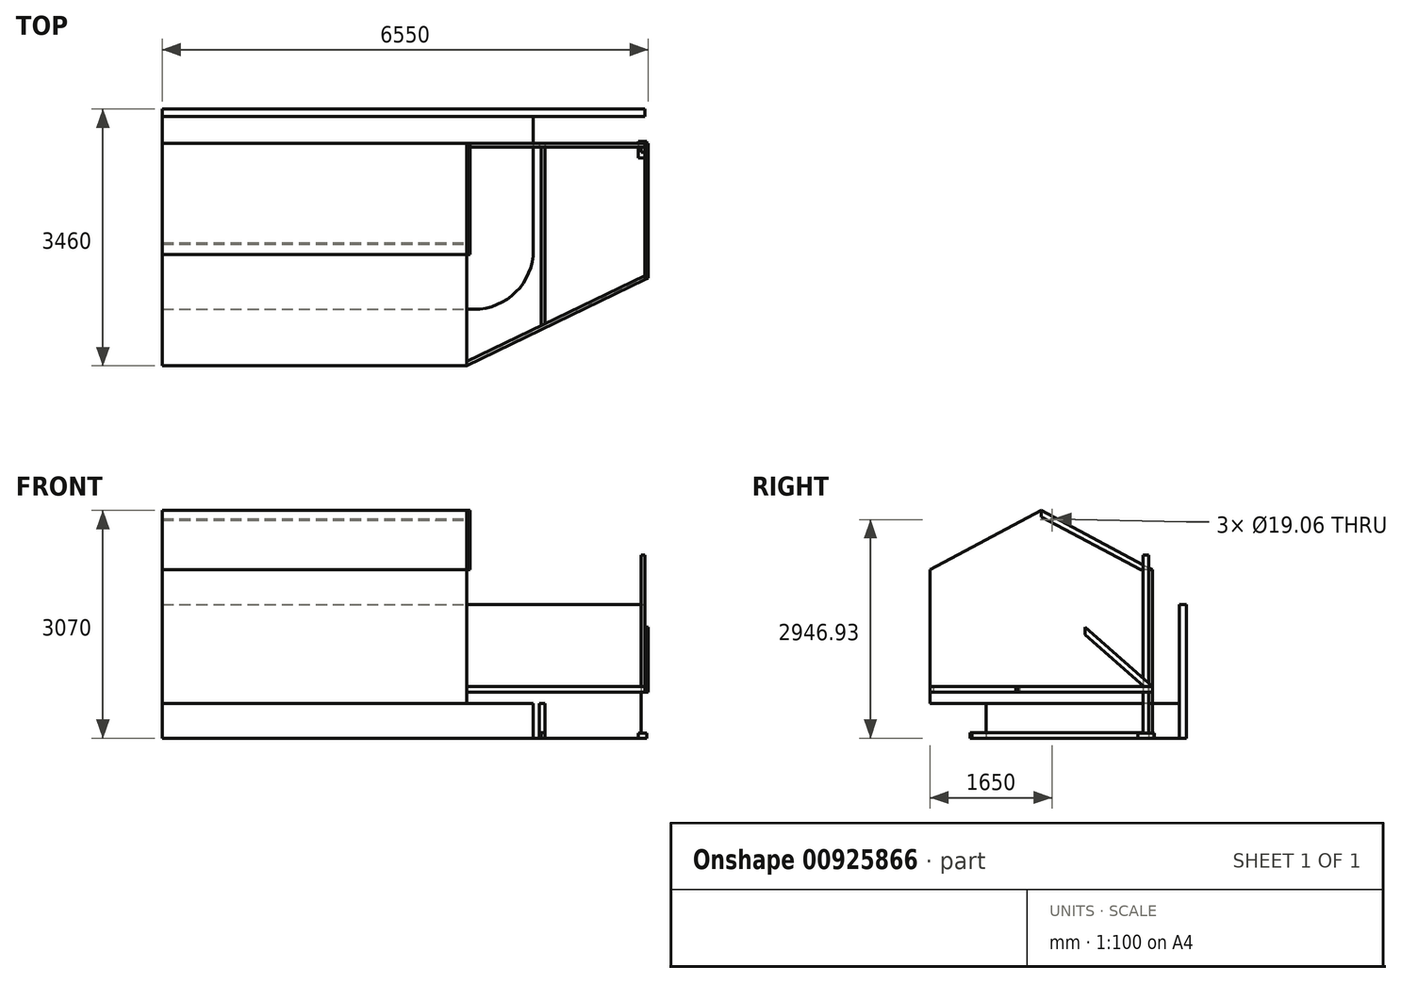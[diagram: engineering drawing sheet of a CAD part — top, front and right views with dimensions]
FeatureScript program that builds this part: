
annotation { "Feature Type Name" : "Feature", "Feature Type Description" : "" }
export const myFeature = defineFeature(function(context is Context, id is Id, definition is map)
    precondition{}
    {
        {
            var Q0;
            Q0=qCreatedBy(makeId("Top.planeOp"),FACE);
            var sketch = newSketch(context, id + "F0", { "sketchPlane" : qUnion([Q0])});
            skLineSegment(sketch, "E0.bottom", {"start": v(0, 0) * mm, "end": v(6500, 0) * mm});
            skLineSegment(sketch, "E0.top", {"start": v(0, 100) * mm, "end": v(6500, 100) * mm});
            skLineSegment(sketch, "E0.left", {"start": v(0, 0) * mm, "end": v(0, 100) * mm});
            skLineSegment(sketch, "E0.right", {"start": v(6500, 0) * mm, "end": v(6500, 100) * mm});
            skSolve(sketch);
        }
        {
            var Q0;
            Q0 = qSketchRegion(id + "F0", true);
            extrude(context, id + "F1", {"entities" : qUnion([Q0]), "depth" : 1800 * mm, "offsetDistance" : 25 * mm});
        }
        {
            var Q0;
            Q0=qCreatedBy(makeId("Top.planeOp"),FACE);
            var sketch = newSketch(context, id + "F2", { "sketchPlane" : qUnion([Q0])});
            skLineSegment(sketch, "E1.bottom", {"start": v(0, 0) * mm, "end": v(5000, 0) * mm});
            skLineSegment(sketch, "E1.top", {"start": v(0, -2600) * mm, "end": v(4200, -2600) * mm});
            skLineSegment(sketch, "E1.left", {"start": v(0, 0) * mm, "end": v(0, -2600) * mm});
            skLineSegment(sketch, "E1.right", {"start": v(5000, 0) * mm, "end": v(5000, -1800) * mm});
            skPoint(sketch, "E2.visualSharp", {"position": v(5000, -2600) * mm});
            skArc(sketch, "E2.filletArc", {"start": v(4200, -2600) * mm, "mid": v(4765.69, -2365.69) * mm, "end": v(5000, -1800) * mm});
            skSolve(sketch);
        }
        {
            var Q0;
            Q0 = qSketchRegion(id + "F2", true);
            extrude(context, id + "F3", {"entities" : qUnion([Q0]), "depth" : 470 * mm, "offsetDistance" : 25 * mm});
        }
        {
            var Q0;
            Q0=makeQuery(id+"F3.opExtrude","CAP_FACE",FACE,{"disambiguationData":[OSD([sQuery(id+"F2.wireOp",EDGE,"E1.bottom"),sQuery(id+"F2.wireOp",EDGE,"E1.top"),sQuery(id+"F2.wireOp",EDGE,"E1.left"),sQuery(id+"F2.wireOp",EDGE,"E1.right"),sQuery(id+"F2.wireOp",EDGE,"E2.filletArc")])],"isStart":false});
            var sketch = newSketch(context, id + "F4", { "sketchPlane" : qUnion([Q0])});
            skLineSegment(sketch, "E3.bottom", {"start": v(0, -3360) * mm, "end": v(4100, -3360) * mm});
            skLineSegment(sketch, "E3.top", {"start": v(0, -360) * mm, "end": v(4100, -360) * mm});
            skLineSegment(sketch, "E3.left", {"start": v(0, -3360) * mm, "end": v(0, -360) * mm});
            skLineSegment(sketch, "E3.right", {"start": v(4100, -3360) * mm, "end": v(4100, -360) * mm});
            skSolve(sketch);
        }
        {
            var Q0;
            Q0 = qSketchRegion(id + "F4", true);
            extrude(context, id + "F5", {"entities" : qUnion([Q0]), "depth" : 1800 * mm, "offsetDistance" : 25 * mm});
        }
        {
            var Q0;
            Q0=makeQuery(id+"F5.opExtrude","SWEPT_FACE",FACE,{"disambiguationData":[OSD([sQuery(id+"F4.wireOp",EDGE,"E3.right")])]});
            var sketch = newSketch(context, id + "F6", { "sketchPlane" : qUnion([Q0])});
            skLineSegment(sketch, "E4", {"start": v(-3360, 2270) * mm, "end": v(-1860, 3070) * mm});
            skPoint(sketch, "E4.endSnap0", {"position": v(-1860, 2270) * mm});
            skLineSegment(sketch, "E5", {"start": v(-1860, 3070) * mm, "end": v(-360, 2270) * mm});
            skLineSegment(sketch, "E6.0", {"start": v(-3360, 2270) * mm, "end": v(-360, 2270) * mm});
            skSolve(sketch);
        }
        {
            var Q0;
            Q0 = qSketchRegion(id + "F6", true);
            var Q1;
            Q1=makeQuery(id+"F5.opExtrude","SWEPT_FACE",FACE,{"disambiguationData":[OSD([sQuery(id+"F4.wireOp",EDGE,"E3.left")])]});
            extrude(context, id + "F7", {"entities" : qUnion([Q0]), "operationType" : NewBodyOperationType.ADD, "endBound" : BoundingType.UP_TO_SURFACE, "oppositeDirection" : true, "depth" : 25 * mm, "endBoundEntityFace" : qUnion([Q1]), "offsetDistance" : 25 * mm});
        }
        {
            var Q0;
            Q0=qCreatedBy(makeId("Top.planeOp"),FACE);
            var sketch = newSketch(context, id + "F8", { "sketchPlane" : qUnion([Q0])});
            skLineSegment(sketch, "E7.bottom", {"start": v(5000, 0) * mm, "end": v(6500, 0) * mm});
            skLineSegment(sketch, "E7.top", {"start": v(5000, -2200) * mm, "end": v(6500, -2200) * mm});
            skLineSegment(sketch, "E7.left", {"start": v(5000, 0) * mm, "end": v(5000, -2200) * mm});
            skLineSegment(sketch, "E7.right", {"start": v(6500, 0) * mm, "end": v(6500, -2200) * mm});
            skLineSegment(sketch, "E8", {"start": v(4100, -3360) * mm, "end": v(6500, -2200) * mm});
            skSolve(sketch);
        }
        {
            var Q0;
            Q0=makeQuery(id+"F7.boolean.opBoolean","MERGE",FACE,{"derivedFrom":[makeQuery(id+"F5.opExtrude","SWEPT_FACE",FACE,{"disambiguationData":[OSD([sQuery(id+"F4.wireOp",EDGE,"E3.right")])]}),makeQuery(id+"F7.opExtrude","CAP_FACE",FACE,{"disambiguationData":[OSD([sQuery(id+"F6.wireOp",EDGE,"E4"),sQuery(id+"F6.wireOp",EDGE,"E5"),sQuery(id+"F6.wireOp",EDGE,"E6.0")])],"isStart":true})]});
            var sketch = newSketch(context, id + "F9", { "sketchPlane" : qUnion([Q0])});
            skLineSegment(sketch, "E9.bottom", {"start": v(-360, 620) * mm, "end": v(-410, 620) * mm});
            skLineSegment(sketch, "E9.top", {"start": v(-360, 696) * mm, "end": v(-410, 696) * mm});
            skLineSegment(sketch, "E9.left", {"start": v(-360, 620) * mm, "end": v(-360, 696) * mm});
            skLineSegment(sketch, "E9.right", {"start": v(-410, 620) * mm, "end": v(-410, 696) * mm});
            skSolve(sketch);
        }
        {
            var Q0;
            Q0 = qSketchRegion(id + "F9", true);
            extrude(context, id + "F10", {"entities" : qUnion([Q0]), "depth" : 2400 * mm, "offsetDistance" : 25 * mm});
        }
        {
            var Q0;
            Q0=makeQuery(id+"F10.opExtrude","SWEPT_FACE",FACE,{"disambiguationData":[OSD([sQuery(id+"F9.wireOp",EDGE,"E9.top")])]});
            var sketch = newSketch(context, id + "F11", { "sketchPlane" : qUnion([Q0])});
            skLineSegment(sketch, "E10", {"start": v(4100, -3304.47) * mm, "end": v(4100, -3360) * mm});
            skLineSegment(sketch, "E11", {"start": v(4100, -3360) * mm, "end": v(6500, -2200) * mm});
            skLineSegment(sketch, "E12", {"start": v(6500, -2200) * mm, "end": v(6500, -2144.47) * mm});
            skLineSegment(sketch, "E13", {"start": v(6500, -2144.47) * mm, "end": v(4100, -3304.47) * mm});
            skSolve(sketch);
        }
        {
            var Q0;
            Q0 = qSketchRegion(id + "F11", true);
            extrude(context, id + "F12", {"entities" : qUnion([Q0]), "oppositeDirection" : true, "depth" : 76 * mm, "offsetDistance" : 25 * mm});
        }
        {
            var Q0;
            Q0=makeQuery(id+"F10.opExtrude","CAP_FACE",FACE,{"disambiguationData":[OSD([sQuery(id+"F9.wireOp",EDGE,"E9.bottom"),sQuery(id+"F9.wireOp",EDGE,"E9.top"),sQuery(id+"F9.wireOp",EDGE,"E9.left"),sQuery(id+"F9.wireOp",EDGE,"E9.right")])],"isStart":false});
            var sketch = newSketch(context, id + "F13", { "sketchPlane" : qUnion([Q0])});
            skLineSegment(sketch, "E14.bottom", {"start": v(-360, 620) * mm, "end": v(-2200, 620) * mm});
            skLineSegment(sketch, "E14.top", {"start": v(-360, 696) * mm, "end": v(-2200, 696) * mm});
            skLineSegment(sketch, "E14.left", {"start": v(-360, 620) * mm, "end": v(-360, 696) * mm});
            skLineSegment(sketch, "E14.right", {"start": v(-2200, 620) * mm, "end": v(-2200, 696) * mm});
            skSolve(sketch);
        }
        {
            var Q0;
            Q0 = qSketchRegion(id + "F13", true);
            extrude(context, id + "F14", {"entities" : qUnion([Q0]), "depth" : 50 * mm, "offsetDistance" : 25 * mm});
        }
        {
            var Q0;
            Q0=qCreatedBy(makeId("Top.planeOp"),FACE);
            var sketch = newSketch(context, id + "F15", { "sketchPlane" : qUnion([Q0])});
            skLineSegment(sketch, "E15.bottom", {"start": v(6526.6, -337.86) * mm, "end": v(6416.6, -337.86) * mm});
            skLineSegment(sketch, "E15.top", {"start": v(6526.6, -557.86) * mm, "end": v(6416.6, -557.86) * mm});
            skLineSegment(sketch, "E15.left", {"start": v(6526.6, -337.86) * mm, "end": v(6526.6, -557.86) * mm});
            skLineSegment(sketch, "E15.right", {"start": v(6416.6, -337.86) * mm, "end": v(6416.6, -557.86) * mm});
            skSolve(sketch);
        }
        {
            var Q0;
            Q0 = qSketchRegion(id + "F15", true);
            extrude(context, id + "F16", {"entities" : qUnion([Q0]), "depth" : 70 * mm, "offsetDistance" : 25 * mm});
        }
        {
            var Q0;
            Q0=makeQuery(id+"F16.opExtrude","CAP_FACE",FACE,{"disambiguationData":[OSD([sQuery(id+"F15.wireOp",EDGE,"E15.bottom"),sQuery(id+"F15.wireOp",EDGE,"E15.top"),sQuery(id+"F15.wireOp",EDGE,"E15.left"),sQuery(id+"F15.wireOp",EDGE,"E15.right")])],"isStart":false});
            var sketch = newSketch(context, id + "F17", { "sketchPlane" : qUnion([Q0])});
            skLineSegment(sketch, "E16.bottom", {"start": v(6500, -410) * mm, "end": v(6450, -410) * mm});
            skLineSegment(sketch, "E16.top", {"start": v(6500, -486) * mm, "end": v(6450, -486) * mm});
            skLineSegment(sketch, "E16.left", {"start": v(6500, -410) * mm, "end": v(6500, -486) * mm});
            skLineSegment(sketch, "E16.right", {"start": v(6450, -410) * mm, "end": v(6450, -486) * mm});
            skSolve(sketch);
        }
        {
            var Q0;
            Q0 = qSketchRegion(id + "F17", true);
            extrude(context, id + "F18", {"entities" : qUnion([Q0]), "depth" : 2400 * mm, "offsetDistance" : 25 * mm});
        }
        {
            var Q0;
            Q0=makeQuery(id+"F7.boolean.opBoolean","MERGE",FACE,{"derivedFrom":[makeQuery(id+"F5.opExtrude","SWEPT_FACE",FACE,{"disambiguationData":[OSD([sQuery(id+"F4.wireOp",EDGE,"E3.right")])]}),makeQuery(id+"F7.opExtrude","CAP_FACE",FACE,{"disambiguationData":[OSD([sQuery(id+"F6.wireOp",EDGE,"E4"),sQuery(id+"F6.wireOp",EDGE,"E5"),sQuery(id+"F6.wireOp",EDGE,"E6.0")])],"isStart":true})]});
            var sketch = newSketch(context, id + "F19", { "sketchPlane" : qUnion([Q0])});
            skLineSegment(sketch, "E17.0", {"start": v(-1860, 3070) * mm, "end": v(-360, 2270) * mm});
            skLineSegment(sketch, "E18.0", {"start": v(-1860, 2983.87) * mm, "end": v(-521.5, 2270) * mm});
            skLineSegment(sketch, "E19", {"start": v(-1860, 3070) * mm, "end": v(-1860, 2983.87) * mm});
            skLineSegment(sketch, "E20", {"start": v(-360, 2270) * mm, "end": v(-521.5, 2270) * mm});
            skSolve(sketch);
        }
        {
            var Q0;
            Q0 = qSketchRegion(id + "F19", true);
            extrude(context, id + "F20", {"entities" : qUnion([Q0]), "depth" : 50 * mm, "offsetDistance" : 25 * mm});
        }
        {
            var Q0;
            Q0=makeQuery(id+"F14.opExtrude","SWEPT_FACE",FACE,{"disambiguationData":[OSD([sQuery(id+"F13.wireOp",EDGE,"E14.top")])]});
            var sketch = newSketch(context, id + "F21", { "sketchPlane" : qUnion([Q0])});
            skLineSegment(sketch, "E21.0", {"start": v(6500, -2200) * mm, "end": v(6550, -2175.83) * mm});
            skLineSegment(sketch, "E22.0", {"start": v(6550, -2175.83) * mm, "end": v(6550, -2200) * mm});
            skLineSegment(sketch, "E23.0", {"start": v(6550, -2200) * mm, "end": v(6500, -2200) * mm});
            skPoint(sketch, "E24.orphan", {"position": v(6500, -2200) * mm});
            skPoint(sketch, "E25.orphan", {"position": v(4100, -3360) * mm});
            skPoint(sketch, "E26.orphan", {"position": v(6550, -360) * mm});
            skSolve(sketch);
        }
        {
            var Q0;
            Q0 = qSketchRegion(id + "F21", true);
            extrude(context, id + "F22", {"entities" : qUnion([Q0]), "operationType" : NewBodyOperationType.REMOVE, "endBound" : BoundingType.THROUGH_ALL, "oppositeDirection" : true, "depth" : 25 * mm, "offsetDistance" : 25 * mm});
        }
        {
            var Q0;
            Q0=makeQuery(id+"F14.opExtrude","CAP_FACE",FACE,{"disambiguationData":[OSD([sQuery(id+"F13.wireOp",EDGE,"E14.bottom"),sQuery(id+"F13.wireOp",EDGE,"E14.top"),sQuery(id+"F13.wireOp",EDGE,"E14.left"),sQuery(id+"F13.wireOp",EDGE,"E14.right")])],"isStart":false});
            var sketch = newSketch(context, id + "F23", { "sketchPlane" : qUnion([Q0])});
            skLineSegment(sketch, "E27", {"start": v(-360, 696) * mm, "end": v(-1267.92, 1496) * mm});
            skLineSegment(sketch, "E28", {"start": v(-1267.92, 1394.7) * mm, "end": v(-474.96, 696) * mm});
            skLineSegment(sketch, "E29.0", {"start": v(-360, 696) * mm, "end": v(-474.96, 696) * mm});
            skPoint(sketch, "E30.orphan", {"position": v(-2175.83, 696) * mm});
            skLineSegment(sketch, "E31", {"start": v(-1267.92, 1394.7) * mm, "end": v(-1267.92, 1496) * mm});
            skPoint(sketch, "E32.orphan", {"position": v(-1267.92, 696) * mm});
            skSolve(sketch);
        }
        {
            var Q0;
            Q0 = qSketchRegion(id + "F23", true);
            extrude(context, id + "F24", {"entities" : qUnion([Q0]), "oppositeDirection" : true, "depth" : 50 * mm, "offsetDistance" : 25 * mm});
        }
        {
            var Q0;
            Q0=qCreatedBy(makeId("Top.planeOp"),FACE);
            var sketch = newSketch(context, id + "F25", { "sketchPlane" : qUnion([Q0])});
            skLineSegment(sketch, "E33.bottom", {"start": v(5080, -360) * mm, "end": v(5156, -360) * mm});
            skLineSegment(sketch, "E33.top", {"start": v(5080, -410) * mm, "end": v(5156, -410) * mm});
            skLineSegment(sketch, "E33.left", {"start": v(5080, -360) * mm, "end": v(5080, -410) * mm});
            skLineSegment(sketch, "E33.right", {"start": v(5156, -360) * mm, "end": v(5156, -410) * mm});
            skSolve(sketch);
        }
        {
            var Q0;
            Q0 = qSketchRegion(id + "F25", true);
            extrude(context, id + "F26", {"entities" : qUnion([Q0]), "depth" : 470 * mm, "offsetDistance" : 25 * mm});
        }
        {
            var Q0;
            Q0=makeQuery(id+"F26.opExtrude","SWEPT_FACE",FACE,{"disambiguationData":[OSD([sQuery(id+"F25.wireOp",EDGE,"E33.top")])]});
            var sketch = newSketch(context, id + "F27", { "sketchPlane" : qUnion([Q0])});
            skLineSegment(sketch, "E34.bottom", {"start": v(5156, 0) * mm, "end": v(5106, 0) * mm});
            skLineSegment(sketch, "E34.top", {"start": v(5156, 76) * mm, "end": v(5106, 76) * mm});
            skLineSegment(sketch, "E34.left", {"start": v(5156, 0) * mm, "end": v(5156, 76) * mm});
            skLineSegment(sketch, "E34.right", {"start": v(5106, 0) * mm, "end": v(5106, 76) * mm});
            skSolve(sketch);
        }
        {
            var Q0;
            Q0 = qSketchRegion(id + "F27", true);
            var Q1;
            Q1=makeQuery(id+"F12.opExtrude","SWEPT_FACE",FACE,{"disambiguationData":[OSD([sQuery(id+"F11.wireOp",EDGE,"E13")])]});
            extrude(context, id + "F28", {"entities" : qUnion([Q0]), "endBound" : BoundingType.UP_TO_SURFACE, "depth" : 25 * mm, "endBoundEntityFace" : qUnion([Q1]), "offsetDistance" : 25 * mm});
        }
        {
            var Q0;
            Q0=makeQuery(id+"F20.opExtrude","CAP_FACE",FACE,{"disambiguationData":[OSD([sQuery(id+"F19.wireOp",EDGE,"E17.0"),sQuery(id+"F19.wireOp",EDGE,"E18.0"),sQuery(id+"F19.wireOp",EDGE,"E19"),sQuery(id+"F19.wireOp",EDGE,"E20")])],"isStart":false});
            var sketch = newSketch(context, id + "F29", { "sketchPlane" : qUnion([Q0])});
            skCircle(sketch, "E35", {"center": v(-1710, 2946.93) * mm, "radius": 9.53 * mm});
            skSolve(sketch);
        }
        {
            var Q0;
            Q0 = qSketchRegion(id + "F29", true);
            extrude(context, id + "F30", {"entities" : qUnion([Q0]), "operationType" : NewBodyOperationType.REMOVE, "endBound" : BoundingType.THROUGH_ALL, "oppositeDirection" : true, "depth" : 25 * mm, "offsetDistance" : 25 * mm});
        }
        {
            var Q0;
            Q0=makeQuery(id+"F3.opExtrude","SWEPT_BODY",BODY,{"disambiguationData":[OSD([sQuery(id+"F2.wireOp",EDGE,"E1.bottom"),sQuery(id+"F2.wireOp",EDGE,"E1.top"),sQuery(id+"F2.wireOp",EDGE,"E1.left"),sQuery(id+"F2.wireOp",EDGE,"E1.right"),sQuery(id+"F2.wireOp",EDGE,"E2.filletArc")])]});
            transform(context, id + "F31", {"entities" : qUnion([Q0]), "transformType" : TransformType.TRANSLATION_3D, "dx" : 0 * mm, "dy" : 0 * mm, "dz" : 0 * mm, "makeCopy" : true});
        }
        {
            var Q0;
            Q0=makeQuery(id+"F5.opExtrude","SWEPT_BODY",BODY,{"disambiguationData":[OSD([sQuery(id+"F4.wireOp",EDGE,"E3.bottom"),sQuery(id+"F4.wireOp",EDGE,"E3.top"),sQuery(id+"F4.wireOp",EDGE,"E3.left"),sQuery(id+"F4.wireOp",EDGE,"E3.right")])]});
            transform(context, id + "F32", {"entities" : qUnion([Q0]), "transformType" : TransformType.TRANSLATION_3D, "dx" : 0 * mm, "dy" : 0 * mm, "dz" : 0 * mm, "makeCopy" : true});
        }
        {
            var Q0;
            Q0=makeQuery(id+"F1.opExtrude","SWEPT_BODY",BODY,{"disambiguationData":[OSD([sQuery(id+"F0.wireOp",EDGE,"E0.bottom"),sQuery(id+"F0.wireOp",EDGE,"E0.top"),sQuery(id+"F0.wireOp",EDGE,"E0.left"),sQuery(id+"F0.wireOp",EDGE,"E0.right")])]});
            transform(context, id + "F33", {"entities" : qUnion([Q0]), "transformType" : TransformType.TRANSLATION_3D, "dx" : 0 * mm, "dy" : 0 * mm, "dz" : 0 * mm, "makeCopy" : true});
        }
    });
